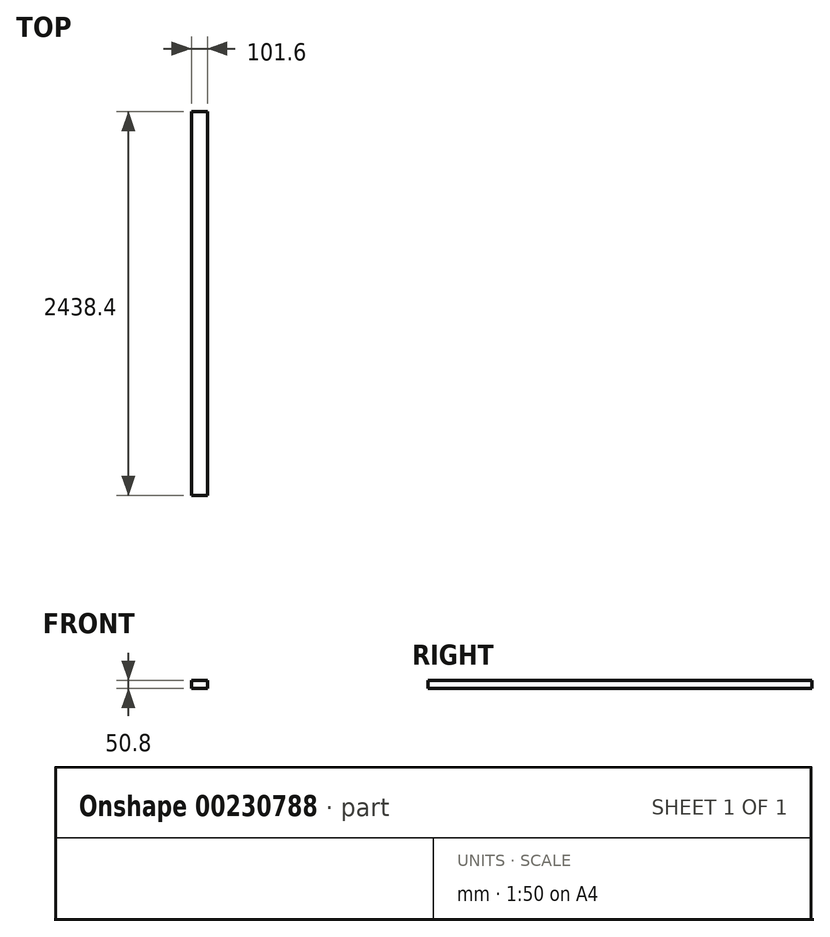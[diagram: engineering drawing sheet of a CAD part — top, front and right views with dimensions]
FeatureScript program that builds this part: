
annotation { "Feature Type Name" : "Feature", "Feature Type Description" : "" }
export const myFeature = defineFeature(function(context is Context, id is Id, definition is map)
    precondition{}
    {
        {
            var Q0;
            Q0=qCreatedBy(makeId("Front.planeOp"),FACE);
            var sketch = newSketch(context, id + "F0", { "sketchPlane" : qUnion([Q0])});
            skLineSegment(sketch, "E0.bottom", {"start": v(-57.36, -23.4) * mm, "end": v(44.24, -23.4) * mm});
            skLineSegment(sketch, "E0.top", {"start": v(-57.36, -74.2) * mm, "end": v(44.24, -74.2) * mm});
            skLineSegment(sketch, "E0.left", {"start": v(-57.36, -23.4) * mm, "end": v(-57.36, -74.2) * mm});
            skLineSegment(sketch, "E0.right", {"start": v(44.24, -23.4) * mm, "end": v(44.24, -74.2) * mm});
            skSolve(sketch);
        }
        {
            var Q0;
            Q0 = qSketchRegion(id + "F0", true);
            extrude(context, id + "F1", {"entities" : qUnion([Q0]), "depth" : 2438.4 * mm});
        }
    });
